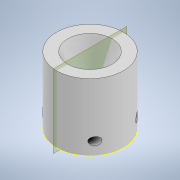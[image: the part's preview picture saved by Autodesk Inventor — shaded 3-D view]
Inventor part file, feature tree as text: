
AUTODESK INVENTOR PART (.ipt)
format: ipt  version: 2020 (Build 240168000, 168)  size: 147,456 bytes
history: native  units: in
note: dims shown in document units (in); Inventor stores cm internally (conversion verified against a paired STEP export)
features: sketch x4, hole x2, revolve x1, plane x1
ambient origin geometry x8: Origin, YZ Plane, XZ Plane, XY Plane, X Axis, Y Axis, Z Axis, Center Point
bodies: Solid1 (feature_tree)
feature tree (8):
  revolve  "Revolution1"  [1 undecoded]
  hole  "Hole1"  [1 undecoded]
  sketch  "Sketch3"  dims[d16=45.0deg d17=90.0deg]
  plane  "Work Plane1"
  hole  "Hole2"  [1 undecoded]
  sketch  "Sketch1"  dims[d7=90.0deg d8=0.211in]
  sketch  "Sketch2"  dims[d10=0.375in d11=0.25in d12=0.5635in d13=0.375in d14=0.0in d15=0.325in]
  sketch  "Sketch4"  dims[d18=0.4in d19=45.0deg d20=0.4in d21=135.0deg d22=0.177in d23=0.328in d24=0.332in d25=0.25in d26=0.5635in d27=0.484in d28=0.8108in]
note: 3 required parameter values undecoded (feature->parameter linkage not recoverable at this tier; creation-order binding heuristic only, values carry confidence <= 0.55)